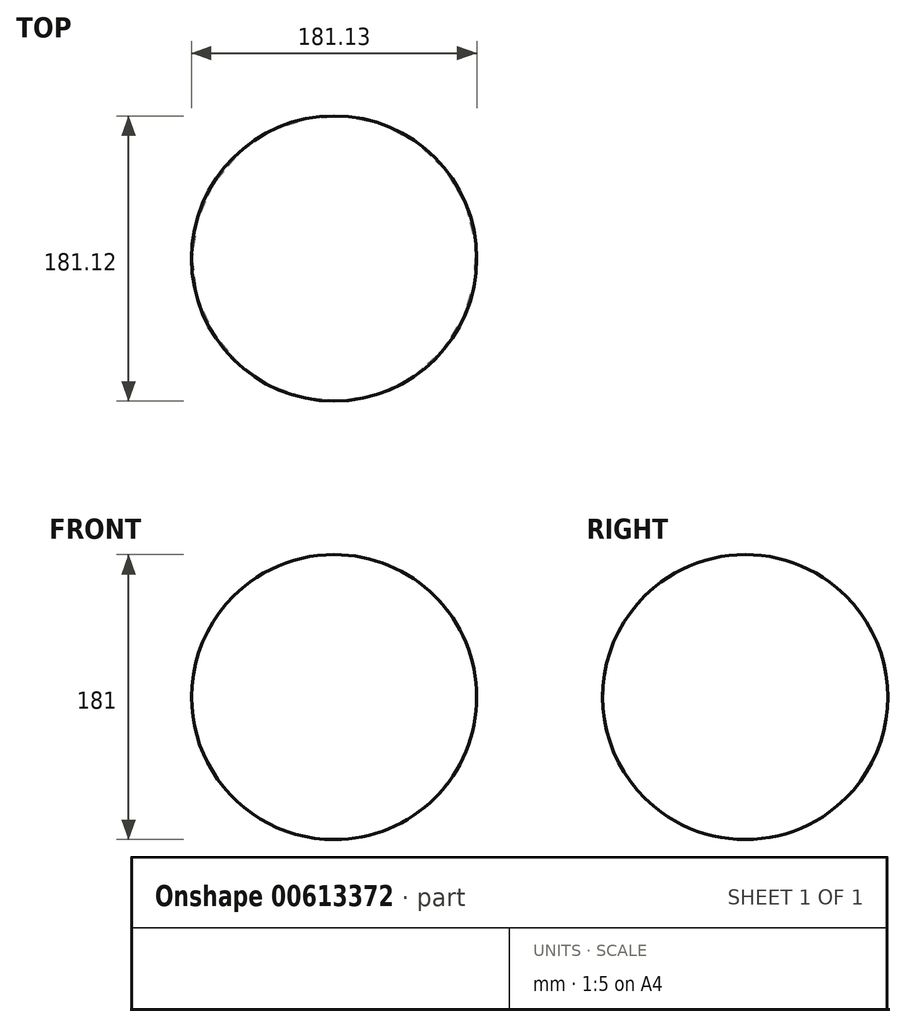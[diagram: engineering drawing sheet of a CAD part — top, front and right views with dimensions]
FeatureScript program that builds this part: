
annotation { "Feature Type Name" : "Feature", "Feature Type Description" : "" }
export const myFeature = defineFeature(function(context is Context, id is Id, definition is map)
    precondition{}
    {
        {
            var Q0;
            Q0=qCreatedBy(makeId("Front.planeOp"),FACE);
            var sketch = newSketch(context, id + "F0", { "sketchPlane" : qUnion([Q0])});
            skArc(sketch, "E0", {"start": v(-37.87, -90.5) * mm, "mid": v(52.57, 0) * mm, "end": v(-37.87, 90.5) * mm});
            skLineSegment(sketch, "E1", {"start": v(-37.87, 90.5) * mm, "end": v(-37.87, -90.5) * mm});
            skSolve(sketch);
        }
        {
            var Q0;
            Q0=makeQuery(id+"F0.imprint","IMPRINT",FACE,{"disambiguationData":[TD([[makeQuery(id+"F0.imprint","IMPRINT",EDGE,{"derivedFrom":sQuery(id+"F0.wireOp",EDGE,"E0")}),1.0]])]});
            var Q1;
            Q1=sQuery(id+"F0.wireOp",EDGE,"E1");
            revolve(context, id + "F1", {"entities" : qUnion([Q0]), "axis" : qUnion([Q1]), "revolveType" : RevolveType.FULL});
        }
    });
